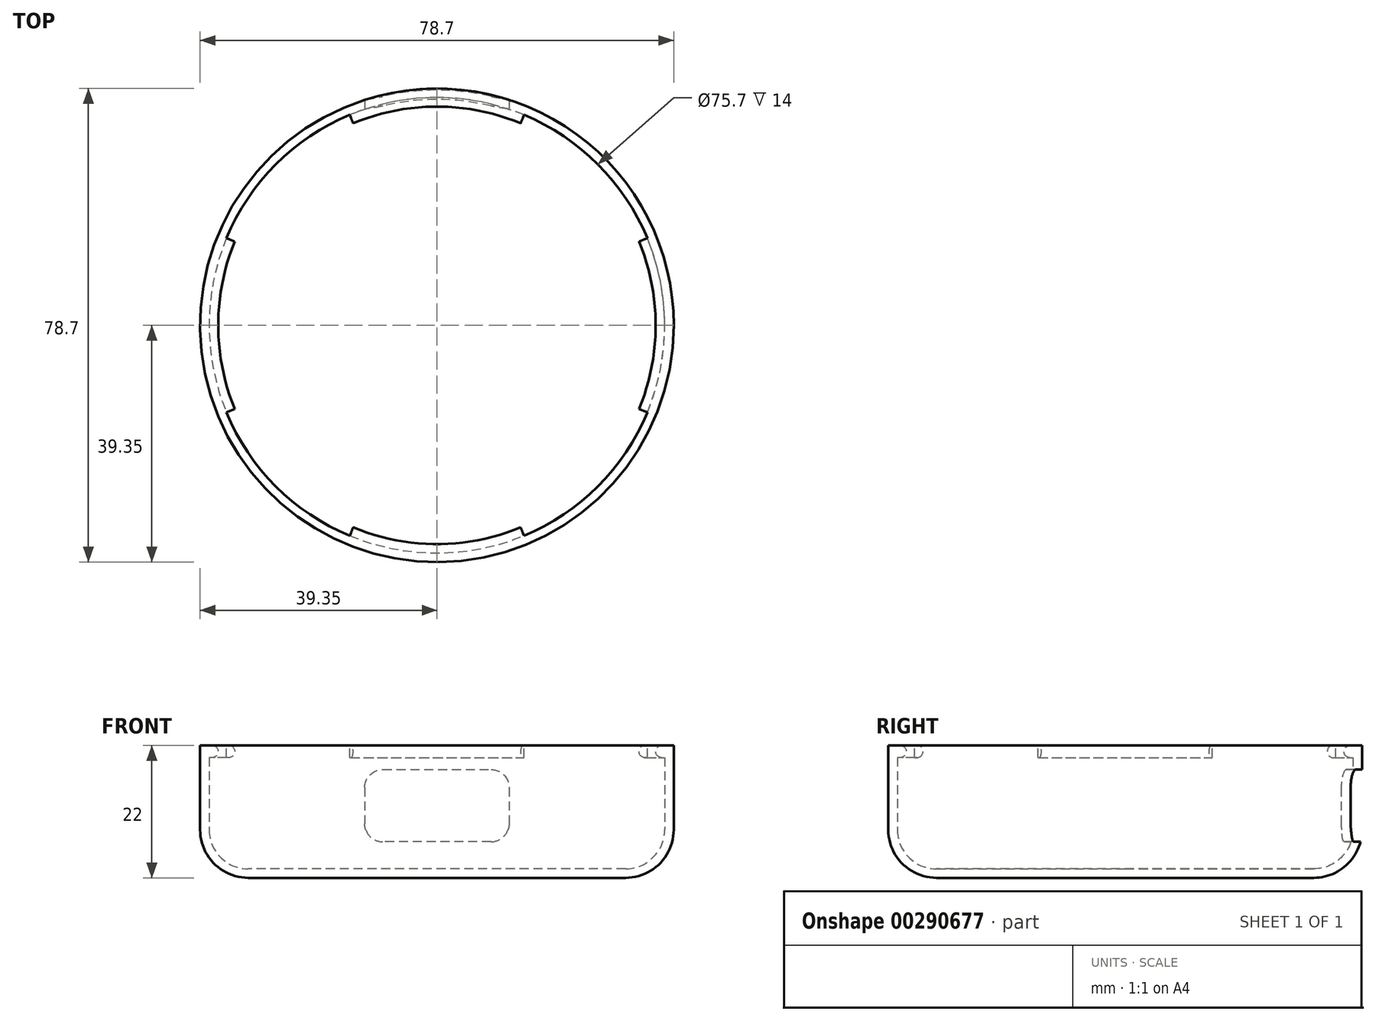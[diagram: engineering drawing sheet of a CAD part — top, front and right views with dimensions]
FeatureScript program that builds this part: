
annotation { "Feature Type Name" : "Feature", "Feature Type Description" : "" }
export const myFeature = defineFeature(function(context is Context, id is Id, definition is map)
    precondition{}
    {
        {
            var Q0;
            Q0=qCreatedBy(makeId("Top.planeOp"),FACE);
            var sketch = newSketch(context, id + "F0", { "sketchPlane" : qUnion([Q0])});
            skCircle(sketch, "E0", {"center": v(0, 0) * mm, "radius": 39.35 * mm});
            skCircle(sketch, "E1.0", {"center": v(0, 0) * mm, "radius": 37.85 * mm});
            skSolve(sketch);
        }
        {
            var Q0;
            Q0=makeQuery(id+"F0.imprint","IMPRINT",FACE,{"disambiguationData":[TD([[makeQuery(id+"F0.imprint","IMPRINT",EDGE,{"derivedFrom":sQuery(id+"F0.wireOp",EDGE,"E0")}),1.0]])]});
            extrude(context, id + "F1", {"entities" : qUnion([Q0]), "depth" : 4 * mm});
        }
        {
            var Q0;
            Q0=makeQuery(id+"F1.opExtrude","CAP_FACE",FACE,{"disambiguationData":[OSD([sQuery(id+"F0.wireOp",EDGE,"E0"),sQuery(id+"F0.wireOp",EDGE,"E1.0")])],"isStart":false});
            var sketch = newSketch(context, id + "F2", { "sketchPlane" : qUnion([Q0])});
            skArc(sketch, "E2.0", {"start": v(34.97, -14.48) * mm, "mid": v(37.85, 0) * mm, "end": v(34.97, 14.48) * mm});
            skPoint(sketch, "E3.0.midPoint", {"position": v(-39.35, 0) * mm});
            skLineSegment(sketch, "E4", {"start": v(-33.58, 13.91) * mm, "end": v(-34.97, 14.48) * mm});
            skLineSegment(sketch, "E5", {"start": v(-34.97, -14.48) * mm, "end": v(-33.58, -13.91) * mm});
            skLineSegment(sketch, "E6", {"start": v(-14.48, -34.97) * mm, "end": v(-13.91, -33.58) * mm});
            skLineSegment(sketch, "E7", {"start": v(34.97, -14.48) * mm, "end": v(33.58, -13.91) * mm});
            skArc(sketch, "E8.0", {"start": v(-13.91, -33.58) * mm, "mid": v(0, -36.35) * mm, "end": v(13.91, -33.58) * mm});
            skLineSegment(sketch, "E9.trimOffspring", {"start": v(13.91, -33.58) * mm, "end": v(14.48, -34.97) * mm});
            skLineSegment(sketch, "E10.trimOffspring", {"start": v(13.91, 33.58) * mm, "end": v(14.48, 34.97) * mm});
            skLineSegment(sketch, "E11.trimOffspring", {"start": v(33.58, 13.91) * mm, "end": v(34.97, 14.48) * mm});
            skLineSegment(sketch, "E12", {"start": v(-14.48, 34.97) * mm, "end": v(-13.91, 33.58) * mm});
            skArc(sketch, "E13.trimOffspring", {"start": v(-33.58, 13.91) * mm, "mid": v(-36.35, 0) * mm, "end": v(-33.58, -13.91) * mm});
            skArc(sketch, "E14.trimOffspring", {"start": v(13.91, 33.58) * mm, "mid": v(0, 36.35) * mm, "end": v(-13.91, 33.58) * mm});
            skArc(sketch, "E15.trimOffspring", {"start": v(33.58, -13.91) * mm, "mid": v(36.35, 0) * mm, "end": v(33.58, 13.91) * mm});
            skArc(sketch, "E16.trimOffspring", {"start": v(-14.48, -34.97) * mm, "mid": v(0, -37.85) * mm, "end": v(14.48, -34.97) * mm});
            skArc(sketch, "E17.trimOffspring", {"start": v(-34.97, 14.48) * mm, "mid": v(-37.85, 0) * mm, "end": v(-34.97, -14.48) * mm});
            skArc(sketch, "E18.trimOffspring", {"start": v(14.48, 34.97) * mm, "mid": v(0, 37.85) * mm, "end": v(-14.48, 34.97) * mm});
            skSolve(sketch);
        }
        {
            var Q0;
            Q0 = qSketchRegion(id + "F2", true);
            extrude(context, id + "F3", {"entities" : qUnion([Q0]), "operationType" : NewBodyOperationType.ADD, "oppositeDirection" : true, "depth" : 2 * mm});
        }
        {
            var Q0;
            Q0=makeQuery(id+"F3.opExtrude","CAP_EDGE",EDGE,{"disambiguationData":[OSD([sQuery(id+"F2.wireOp",EDGE,"E14.trimOffspring")])],"isStart":false});
            var Q1;
            Q1=makeQuery(id+"F3.opExtrude","CAP_EDGE",EDGE,{"disambiguationData":[OSD([sQuery(id+"F2.wireOp",EDGE,"E14.trimOffspring")])],"isStart":true});
            var Q2;
            Q2=makeQuery(id+"F3.opExtrude","CAP_EDGE",EDGE,{"disambiguationData":[OSD([sQuery(id+"F2.wireOp",EDGE,"E15.trimOffspring")])],"isStart":true});
            var Q3;
            Q3=makeQuery(id+"F3.opExtrude","CAP_EDGE",EDGE,{"disambiguationData":[OSD([sQuery(id+"F2.wireOp",EDGE,"E15.trimOffspring")])],"isStart":false});
            var Q4;
            Q4=makeQuery(id+"F3.opExtrude","CAP_EDGE",EDGE,{"disambiguationData":[OSD([sQuery(id+"F2.wireOp",EDGE,"E8.0")])],"isStart":true});
            var Q5;
            Q5=makeQuery(id+"F3.opExtrude","CAP_EDGE",EDGE,{"disambiguationData":[OSD([sQuery(id+"F2.wireOp",EDGE,"E8.0")])],"isStart":false});
            var Q6;
            Q6=makeQuery(id+"F3.opExtrude","CAP_EDGE",EDGE,{"disambiguationData":[OSD([sQuery(id+"F2.wireOp",EDGE,"E13.trimOffspring")])],"isStart":true});
            var Q7;
            Q7=makeQuery(id+"F3.opExtrude","CAP_EDGE",EDGE,{"disambiguationData":[OSD([sQuery(id+"F2.wireOp",EDGE,"E13.trimOffspring")])],"isStart":false});
            fillet(context, id + "F4", {"entities" : qUnion([Q0, Q1, Q2, Q3, Q4, Q5, Q6, Q7]), "radius" : 1 * mm, "tangentPropagation" : true, "allowEdgeOverflow" : false});
        }
        {
            var Q0;
            Q0=qCreatedBy(makeId("Front.planeOp"),FACE);
            var sketch = newSketch(context, id + "F5", { "sketchPlane" : qUnion([Q0])});
            skLineSegment(sketch, "E19", {"start": v(0, 0) * mm, "end": v(0, -18) * mm});
            skLineSegment(sketch, "E20", {"start": v(-39.35, 0) * mm, "end": v(-39.35, 4) * mm});
            skLineSegment(sketch, "E21", {"start": v(0, -18) * mm, "end": v(-31.35, -18) * mm});
            skLineSegment(sketch, "E22", {"start": v(-39.35, -10) * mm, "end": v(-39.35, 0) * mm});
            skLineSegment(sketch, "E23", {"start": v(-39.35, 0) * mm, "end": v(-32.35, 0) * mm});
            skLineSegment(sketch, "E24", {"start": v(-32.35, 0) * mm, "end": v(-32.35, -14) * mm});
            skLineSegment(sketch, "E25", {"start": v(-32.35, -14) * mm, "end": v(-29.35, -14) * mm});
            skLineSegment(sketch, "E26", {"start": v(-29.35, -14) * mm, "end": v(-29.35, 0) * mm});
            skPoint(sketch, "E27.visualSharp", {"position": v(-39.35, -18) * mm});
            skArc(sketch, "E27.filletArc", {"start": v(-39.35, -10) * mm, "mid": v(-37, -15.66) * mm, "end": v(-31.35, -18) * mm});
            skLineSegment(sketch, "E28.0", {"start": v(-37.85, -10) * mm, "end": v(-37.85, 0) * mm});
            skArc(sketch, "E28.1", {"start": v(-37.85, -10) * mm, "mid": v(-35.95, -14.6) * mm, "end": v(-31.35, -16.5) * mm});
            skLineSegment(sketch, "E28.2", {"start": v(0, -16.5) * mm, "end": v(-31.35, -16.5) * mm});
            skSolve(sketch);
        }
        {
            var Q0;
            {var subQ3=sQuery(id+"F5.wireOp",EDGE,"E21");Q0=makeQuery(id+"F5.imprint","IMPRINT",FACE,{"disambiguationData":[TD([[makeQuery(id+"F5.imprint","IMPRINT",EDGE,{"derivedFrom":subQ3}),-1.0]])]});}
            var Q1;
            Q1=sQuery(id+"F5.wireOp",EDGE,"E19");
            revolve(context, id + "F6", {"operationType" : NewBodyOperationType.ADD, "entities" : qUnion([Q0]), "axis" : qUnion([Q1]), "revolveType" : RevolveType.FULL});
        }
        {
            var Q0;
            Q0=qCreatedBy(makeId("Front.planeOp"),FACE);
            var sketch = newSketch(context, id + "F7", { "sketchPlane" : qUnion([Q0])});
            skLineSegment(sketch, "E29", {"start": v(0, 0) * mm, "end": v(12, 0) * mm});
            skLineSegment(sketch, "E30", {"start": v(12, 0) * mm, "end": v(12, -12) * mm});
            skLineSegment(sketch, "E31", {"start": v(12, -12) * mm, "end": v(-12, -12) * mm});
            skLineSegment(sketch, "E32", {"start": v(-12, -12) * mm, "end": v(-12, 0) * mm});
            skLineSegment(sketch, "E33", {"start": v(-12, 0) * mm, "end": v(0, 0) * mm});
            skSolve(sketch);
        }
        {
            var Q0;
            Q0 = qSketchRegion(id + "F7", true);
            extrude(context, id + "F8", {"entities" : qUnion([Q0]), "operationType" : NewBodyOperationType.REMOVE, "oppositeDirection" : true, "depth" : 72 * mm});
        }
        {
            var Q0;
            Q0=makeQuery(id+"F8.boolean.opBoolean","COPY",EDGE,{"derivedFrom":makeQuery(id+"F8.opExtrude","SWEPT_EDGE",EDGE,{"disambiguationData":[OSD([sQuery(id+"F7.wireOp",EDGE,"E31"),sQuery(id+"F7.wireOp",EDGE,"E32")])]})});
            var Q1;
            Q1=makeQuery(id+"F8.boolean.opBoolean","COPY",EDGE,{"derivedFrom":makeQuery(id+"F8.opExtrude","SWEPT_EDGE",EDGE,{"disambiguationData":[OSD([sQuery(id+"F7.wireOp",EDGE,"E32"),sQuery(id+"F7.wireOp",EDGE,"E33")])]})});
            var Q2;
            Q2=makeQuery(id+"F8.boolean.opBoolean","COPY",EDGE,{"derivedFrom":makeQuery(id+"F8.opExtrude","SWEPT_EDGE",EDGE,{"disambiguationData":[OSD([sQuery(id+"F7.wireOp",EDGE,"E29"),sQuery(id+"F7.wireOp",EDGE,"E30")])]})});
            var Q3;
            Q3=makeQuery(id+"F8.boolean.opBoolean","COPY",EDGE,{"derivedFrom":makeQuery(id+"F8.opExtrude","SWEPT_EDGE",EDGE,{"disambiguationData":[OSD([sQuery(id+"F7.wireOp",EDGE,"E30"),sQuery(id+"F7.wireOp",EDGE,"E31")])]})});
            fillet(context, id + "F9", {"entities" : qUnion([Q0, Q1, Q2, Q3]), "radius" : 3 * mm, "tangentPropagation" : true, "allowEdgeOverflow" : false});
        }
    });
